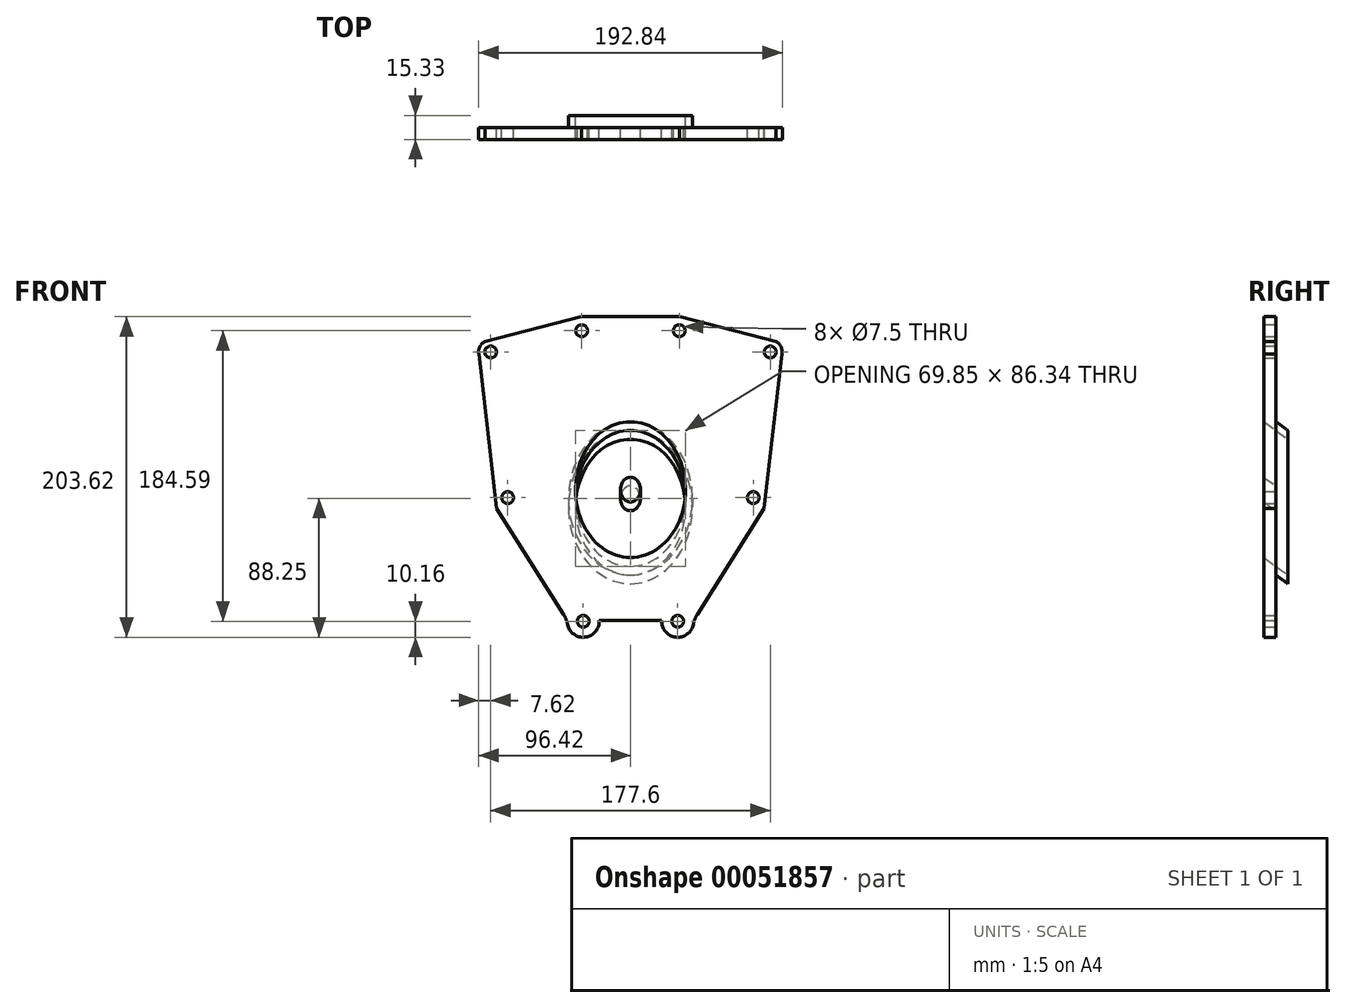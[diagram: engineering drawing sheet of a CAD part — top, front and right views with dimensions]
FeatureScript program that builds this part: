
annotation { "Feature Type Name" : "Feature", "Feature Type Description" : "" }
export const myFeature = defineFeature(function(context is Context, id is Id, definition is map)
    precondition{}
    {
        {
            var Q0;
            Q0=qCreatedBy(makeId("Front.planeOp"),FACE);
            var sketch = newSketch(context, id + "F0", { "sketchPlane" : qUnion([Q0])});
            skCircle(sketch, "E0", {"center": v(31, 106.5) * mm, "radius": 3.75 * mm});
            skCircle(sketch, "E1", {"center": v(88.8, 92.95) * mm, "radius": 3.75 * mm});
            skCircle(sketch, "E2", {"center": v(78, 0.46) * mm, "radius": 3.75 * mm});
            skCircle(sketch, "E3", {"center": v(30, -78.09) * mm, "radius": 3.75 * mm});
            skArc(sketch, "E4.filletArc", {"start": v(19.86, -77.42) * mm, "mid": v(28.72, -88.17) * mm, "end": v(39.98, -79.97) * mm});
            skPoint(sketch, "E5.visualSharp", {"position": v(103.95, 103.85) * mm});
            skArc(sketch, "E5.filletArc", {"start": v(96.32, 91.7) * mm, "mid": v(95.64, 96.3) * mm, "end": v(92.43, 99.65) * mm});
            skCircle(sketch, "E6.MirrorC", {"center": v(-78, 0.46) * mm, "radius": 3.75 * mm});
            skCircle(sketch, "E7.MirrorC", {"center": v(-30, -78.09) * mm, "radius": 3.75 * mm});
            skLineSegment(sketch, "E8", {"start": v(31, 115.37) * mm, "end": v(92.43, 99.65) * mm});
            skLineSegment(sketch, "E9", {"start": v(84.94, -6.57) * mm, "end": v(42.43, -73.77) * mm});
            skLineSegment(sketch, "E10.MirrorCS", {"start": v(-84.94, -6.57) * mm, "end": v(-42.43, -73.77) * mm});
            skArc(sketch, "E11.MirrorCS", {"start": v(-19.86, -77.42) * mm, "mid": v(-28.72, -88.17) * mm, "end": v(-39.98, -79.97) * mm});
            skLineSegment(sketch, "E12", {"start": v(-19.86, -77.42) * mm, "end": v(19.86, -77.42) * mm});
            skPoint(sketch, "E13.visualSharp", {"position": v(40.14, -77.4) * mm});
            skArc(sketch, "E13.filletArc", {"start": v(42.43, -73.77) * mm, "mid": v(40.91, -76.75) * mm, "end": v(39.98, -79.97) * mm});
            skPoint(sketch, "E14.visualSharp", {"position": v(-40.14, -77.4) * mm});
            skArc(sketch, "E14.filletArc", {"start": v(-39.98, -79.97) * mm, "mid": v(-40.91, -76.75) * mm, "end": v(-42.43, -73.77) * mm});
            skCircle(sketch, "E15.MirrorC", {"center": v(-31, 106.5) * mm, "radius": 3.75 * mm});
            skCircle(sketch, "E16.MirrorC", {"center": v(-88.8, 92.95) * mm, "radius": 3.75 * mm});
            skLineSegment(sketch, "E17", {"start": v(-88.8, 92.95) * mm, "end": v(88.8, 92.95) * mm});
            skLineSegment(sketch, "E18", {"start": v(96.32, 91.7) * mm, "end": v(84.94, -6.57) * mm});
            skLineSegment(sketch, "E19.MirrorCS", {"start": v(-31, 115.37) * mm, "end": v(-92.43, 99.65) * mm});
            skArc(sketch, "E20.MirrorCS", {"start": v(-96.32, 91.7) * mm, "mid": v(-95.64, 96.3) * mm, "end": v(-92.43, 99.65) * mm});
            skLineSegment(sketch, "E21.MirrorCS", {"start": v(-96.32, 91.7) * mm, "end": v(-84.94, -6.57) * mm});
            skLineSegment(sketch, "E22", {"start": v(31, 115.37) * mm, "end": v(-31, 115.37) * mm});
            skLineSegment(sketch, "E23", {"start": v(-88.8, 92.95) * mm, "end": v(-88.8, 0.46) * mm, "construction": true});
            skLineSegment(sketch, "E24", {"start": v(-30, -78.09) * mm, "end": v(-30, 0) * mm, "construction": true});
            skSolve(sketch);
        }
        {
            var Q0;
            Q0 = qSketchRegion(id + "F0", true);
            extrude(context, id + "F1", {"entities" : qUnion([Q0]), "depth" : 7.62 * mm});
        }
        {
            var Q0;
            Q0=makeQuery(id+"F1.opExtrude","CAP_EDGE",EDGE,{"disambiguationData":[OSD([sQuery(id+"F0.wireOp",EDGE,"E12")])],"isStart":true});
            cPlane(context, id + "F2", {"entities" : qUnion([Q0]), "cplaneType" : CPlaneType.LINE_ANGLE, "offset" : 152.4 * mm, "angle" : 324 * degree, "width" : 152.4 * mm, "height" : 152.4 * mm});
        }
        {
            var Q0;
            Q0=qCreatedBy(id+"F2.planeOp",FACE);
            var sketch = newSketch(context, id + "F3", { "sketchPlane" : qUnion([Q0])});
            skCircle(sketch, "E25", {"center": v(0, 0) * mm, "radius": 34.93 * mm});
            skCircle(sketch, "E26", {"center": v(0, 0) * mm, "radius": 39.37 * mm});
            skSolve(sketch);
        }
        {
            var Q0;
            Q0 = qSketchRegion(id + "F3", true);
            var Q1;
            Q1=makeQuery(id+"F1.opExtrude","CAP_FACE",FACE,{"disambiguationData":[OSD([sQuery(id+"F0.wireOp",EDGE,"E0"),sQuery(id+"F0.wireOp",EDGE,"E1"),sQuery(id+"F0.wireOp",EDGE,"E2"),sQuery(id+"F0.wireOp",EDGE,"E3"),sQuery(id+"F0.wireOp",EDGE,"E4.filletArc"),sQuery(id+"F0.wireOp",EDGE,"E5.filletArc"),sQuery(id+"F0.wireOp",EDGE,"E6.MirrorC"),sQuery(id+"F0.wireOp",EDGE,"E7.MirrorC"),sQuery(id+"F0.wireOp",EDGE,"E8"),sQuery(id+"F0.wireOp",EDGE,"E9"),sQuery(id+"F0.wireOp",EDGE,"7f39cb56-5eae-4376-9c15-393519846fc2.filletArc"),sQuery(id+"F0.wireOp",EDGE,"28841198-a3b0-4a59-a94a-61954dabee520.MirrorCS"),sQuery(id+"F0.wireOp",EDGE,"E10.MirrorCS"),sQuery(id+"F0.wireOp",EDGE,"E11.MirrorCS"),sQuery(id+"F0.wireOp",EDGE,"E12"),sQuery(id+"F0.wireOp",EDGE,"E13.filletArc"),sQuery(id+"F0.wireOp",EDGE,"E14.filletArc"),sQuery(id+"F0.wireOp",EDGE,"35c47b91-e903-4fa7-9931-186abe9d42520.MirrorCS"),sQuery(id+"F0.wireOp",EDGE,"58c34199-2d0c-40f7-b25a-44c36ae67cd80.MirrorCS"),sQuery(id+"F0.wireOp",EDGE,"E15.MirrorC"),sQuery(id+"F0.wireOp",EDGE,"E16.MirrorC"),sQuery(id+"F0.wireOp",EDGE,"65c45519-3366-45d4-8366-c42a1005aa8a"),sQuery(id+"F0.wireOp",EDGE,"7c29e703-25ef-44ff-8068-2acf41113fa5"),sQuery(id+"F0.wireOp",EDGE,"d68e92ea-989b-4906-b2b1-d996b8a09dc1"),sQuery(id+"F0.wireOp",EDGE,"aa00a4bb-6105-4af6-b32c-6f9ecd39f326")])],"isStart":true});
            extrude(context, id + "F4", {"entities" : qUnion([Q0]), "endBound" : BoundingType.UP_TO_SURFACE, "oppositeDirection" : true, "endBoundEntityFace" : qUnion([Q1]), "depth" : 76.2 * mm});
        }
        {
            var Q0;
            Q0=qCreatedBy(id+"F2.planeOp",FACE);
            var sketch = newSketch(context, id + "F5", { "sketchPlane" : qUnion([Q0])});
            skCircle(sketch, "E27", {"center": v(0, 0) * mm, "radius": 34.92 * mm});
            skCircle(sketch, "E28", {"center": v(0, 0) * mm, "radius": 6.35 * mm});
            skSolve(sketch);
        }
        {
            var Q0;
            Q0 = qSketchRegion(id + "F5", true);
            extrude(context, id + "F6", {"entities" : qUnion([Q0]), "operationType" : NewBodyOperationType.REMOVE, "endBound" : BoundingType.THROUGH_ALL, "oppositeDirection" : true, "depth" : 25.4 * mm});
        }
        {
            var Q0;
            Q0=qCreatedBy(makeId("Right.planeOp"),FACE);
            var sketch = newSketch(context, id + "F7", { "sketchPlane" : qUnion([Q0])});
            skLineSegment(sketch, "E29.bottom", {"start": v(7.71, 44.63) * mm, "end": v(71.7, 44.63) * mm});
            skLineSegment(sketch, "E29.top", {"start": v(7.71, -78.35) * mm, "end": v(71.7, -78.35) * mm});
            skLineSegment(sketch, "E29.left", {"start": v(7.71, 44.63) * mm, "end": v(7.71, -78.35) * mm});
            skLineSegment(sketch, "E29.right", {"start": v(71.7, 44.63) * mm, "end": v(71.7, -78.35) * mm});
            skSolve(sketch);
        }
        {
            var Q0;
            Q0 = qSketchRegion(id + "F7", true);
            extrude(context, id + "F8", {"entities" : qUnion([Q0]), "operationType" : NewBodyOperationType.REMOVE, "oppositeDirection" : true, "depth" : 50.8 * mm, "hasSecondDirection" : true, "secondDirectionOppositeDirection" : false, "secondDirectionDepth" : 50.8 * mm});
        }
    });
